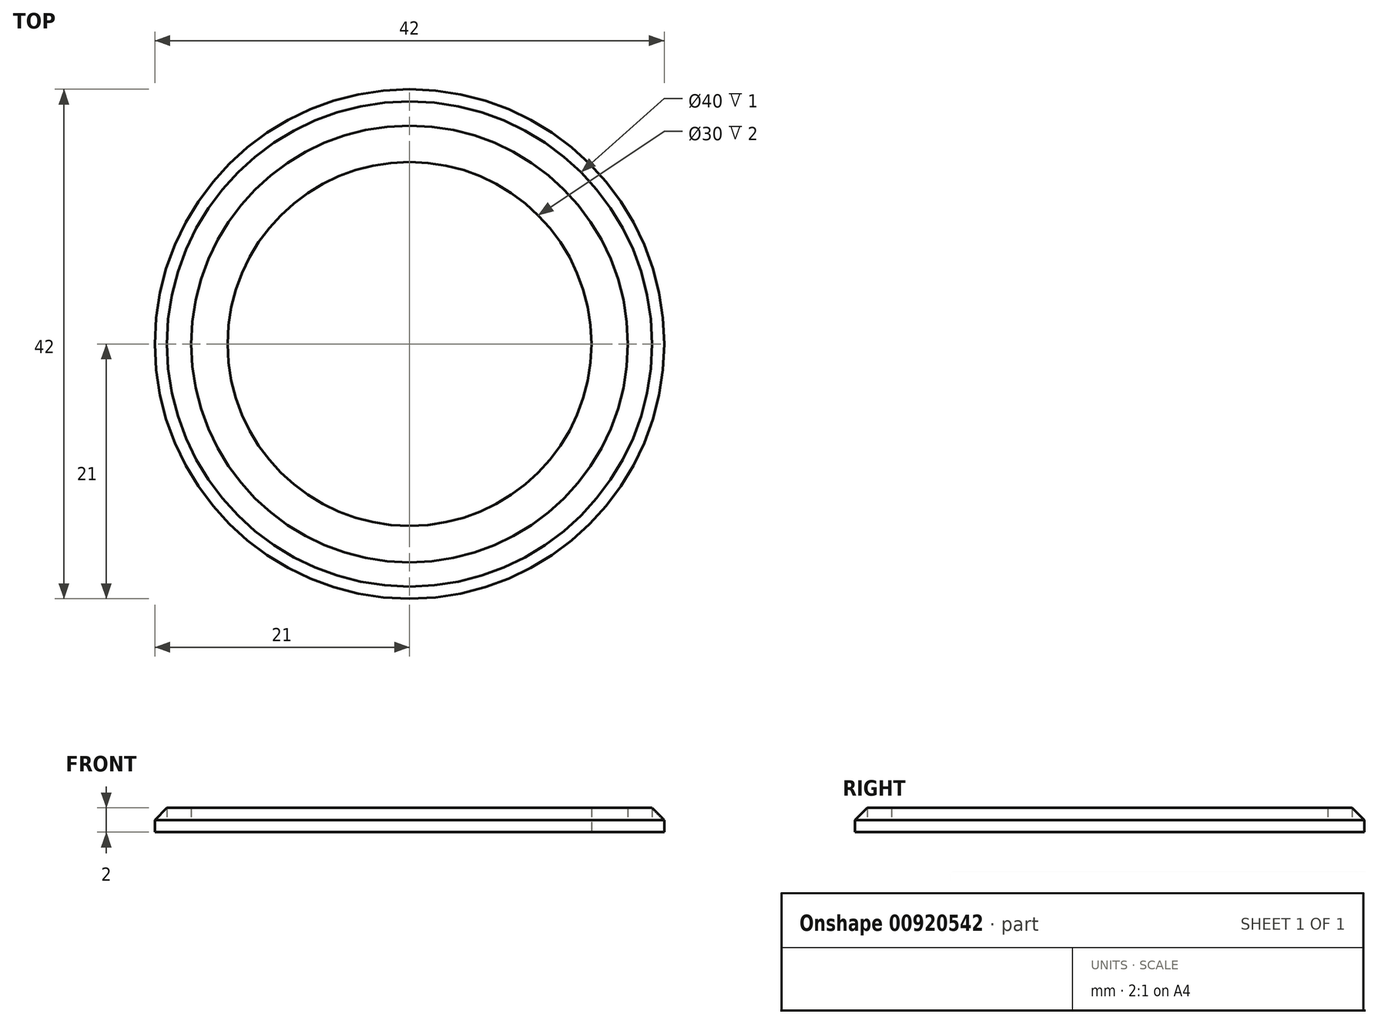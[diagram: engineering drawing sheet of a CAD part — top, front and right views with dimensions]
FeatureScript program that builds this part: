
annotation { "Feature Type Name" : "Feature", "Feature Type Description" : "" }
export const myFeature = defineFeature(function(context is Context, id is Id, definition is map)
    precondition{}
    {
        {
            var Q0;
            Q0=qCreatedBy(makeId("Top.planeOp"),FACE);
            var sketch = newSketch(context, id + "F0", { "sketchPlane" : qUnion([Q0])});
            skCircle(sketch, "E0", {"center": v(0, 0) * mm, "radius": 21 * mm});
            skCircle(sketch, "E1", {"center": v(0, 0) * mm, "radius": 20 * mm});
            skCircle(sketch, "E2", {"center": v(0, 0) * mm, "radius": 18 * mm});
            skCircle(sketch, "E3", {"center": v(0, 0) * mm, "radius": 15 * mm});
            skLineSegment(sketch, "E4", {"start": v(-21, 0) * mm, "end": v(-18, 0) * mm});
            skLineSegment(sketch, "E5", {"start": v(-18, 0) * mm, "end": v(-17.3, 0) * mm});
            skLineSegment(sketch, "E6", {"start": v(-16.5, 0) * mm, "end": v(-16.5, -2) * mm, "construction": true});
            skLineSegment(sketch, "E7", {"start": v(-16.5, -2) * mm, "end": v(-15.5, -2) * mm});
            skLineSegment(sketch, "E8", {"start": v(-15.5, -2) * mm, "end": v(-15.7, 0) * mm});
            skLineSegment(sketch, "E9.MirrorCS", {"start": v(-16.5, -2) * mm, "end": v(-17.5, -2) * mm});
            skLineSegment(sketch, "E10.MirrorCS", {"start": v(-17.5, -2) * mm, "end": v(-17.3, 0) * mm});
            skLineSegment(sketch, "E11.trimOffspring", {"start": v(-15.7, 0) * mm, "end": v(-15, 0) * mm});
            skLineSegment(sketch, "E12", {"start": v(0, 0) * mm, "end": v(0, -15) * mm, "construction": true});
            skLineSegment(sketch, "E13.MirrorCS", {"start": v(15.5, -2) * mm, "end": v(15.7, 0) * mm});
            skLineSegment(sketch, "E14.MirrorCS", {"start": v(16.5, -2) * mm, "end": v(15.5, -2) * mm});
            skLineSegment(sketch, "E15.MirrorCS", {"start": v(16.5, -2) * mm, "end": v(17.5, -2) * mm});
            skLineSegment(sketch, "E16.MirrorCS", {"start": v(17.5, -2) * mm, "end": v(17.3, 0) * mm});
            skLineSegment(sketch, "E17.MirrorCS", {"start": v(21, 0) * mm, "end": v(18, 0) * mm});
            skLineSegment(sketch, "E18.MirrorCS", {"start": v(18, 0) * mm, "end": v(17.3, 0) * mm});
            skLineSegment(sketch, "E19.MirrorCS", {"start": v(15.7, 0) * mm, "end": v(15, 0) * mm});
            skSolve(sketch);
        }
        {
            var Q0;
            {var subQ0=sQuery(id+"F0.wireOp",EDGE,"E4");var subQ1=sQuery(id+"F0.wireOp",EDGE,"E0");var subQ2=makeQuery(id+"F0.imprint","INTERSECT",VERTEX,{"derivedFrom":[subQ1,subQ0]});Q0=makeQuery(id+"F0.imprint","IMPRINT",FACE,{"disambiguationData":[TD([[makeQuery(id+"F0.imprint","IMPRINT",EDGE,{"disambiguationData":[TD([[subQ2,1.0]])],"derivedFrom":subQ1}),1.0]])]});}
            extrude(context, id + "F1", {"entities" : qUnion([Q0]), "depth" : 2 * mm, "offsetDistance" : 25 * mm});
        }
        {
            var Q0;
            {var subQ0=sQuery(id+"F0.wireOp",EDGE,"E4");var subQ1=sQuery(id+"F0.wireOp",EDGE,"E1");var subQ2=makeQuery(id+"F0.imprint","INTERSECT",VERTEX,{"derivedFrom":[subQ1,subQ0]});Q0=makeQuery(id+"F0.imprint","IMPRINT",FACE,{"disambiguationData":[TD([[makeQuery(id+"F0.imprint","IMPRINT",EDGE,{"disambiguationData":[TD([[subQ2,1.0]])],"derivedFrom":subQ1}),1.0]])]});}
            extrude(context, id + "F2", {"entities" : qUnion([Q0]), "operationType" : NewBodyOperationType.ADD, "depth" : 1 * mm, "offsetDistance" : 25 * mm});
        }
        {
            var Q0;
            {var subQ1=sQuery(id+"F0.wireOp",EDGE,"E5");Q0=makeQuery(id+"F0.imprint","IMPRINT",FACE,{"disambiguationData":[TD([[makeQuery(id+"F0.imprint","IMPRINT",EDGE,{"derivedFrom":subQ1}),1.0]])]});}
            extrude(context, id + "F3", {"entities" : qUnion([Q0]), "operationType" : NewBodyOperationType.ADD, "depth" : 2 * mm, "offsetDistance" : 25 * mm});
        }
        {
            var Q0;
            {var subQ1=sQuery(id+"F0.wireOp",EDGE,"E5");Q0=makeQuery(id+"F0.imprint","IMPRINT",FACE,{"disambiguationData":[TD([[makeQuery(id+"F0.imprint","IMPRINT",EDGE,{"derivedFrom":subQ1}),-1.0]])]});}
            extrude(context, id + "F4", {"entities" : qUnion([Q0]), "depth" : 2 * mm, "offsetDistance" : 25 * mm});
        }
        {
            var Q0;
            {var subQ0=sQuery(id+"F0.wireOp",EDGE,"E4");var subQ1=sQuery(id+"F0.wireOp",EDGE,"E1");var subQ2=makeQuery(id+"F0.imprint","INTERSECT",VERTEX,{"derivedFrom":[subQ1,subQ0]});Q0=makeQuery(id+"F0.imprint","IMPRINT",FACE,{"disambiguationData":[TD([[makeQuery(id+"F0.imprint","IMPRINT",EDGE,{"disambiguationData":[TD([[subQ2,-1.0]])],"derivedFrom":subQ1}),1.0]])]});}
            extrude(context, id + "F5", {"entities" : qUnion([Q0]), "operationType" : NewBodyOperationType.ADD, "depth" : 1 * mm, "offsetDistance" : 25 * mm});
        }
        {
            var Q0;
            {var subQ0=sQuery(id+"F0.wireOp",EDGE,"E4");var subQ1=sQuery(id+"F0.wireOp",EDGE,"E0");var subQ2=makeQuery(id+"F0.imprint","INTERSECT",VERTEX,{"derivedFrom":[subQ1,subQ0]});Q0=makeQuery(id+"F0.imprint","IMPRINT",FACE,{"disambiguationData":[TD([[makeQuery(id+"F0.imprint","IMPRINT",EDGE,{"disambiguationData":[TD([[subQ2,-1.0]])],"derivedFrom":subQ1}),1.0]])]});}
            extrude(context, id + "F6", {"entities" : qUnion([Q0]), "operationType" : NewBodyOperationType.ADD, "depth" : 2 * mm, "offsetDistance" : 25 * mm});
        }
        {
            var Q0;
            Q0=makeQuery(id+"F6.opExtrude","CAP_EDGE",EDGE,{"disambiguationData":[OSD([sQuery(id+"F0.wireOp",EDGE,"E0")])],"isStart":false});
            var Q1;
            Q1=makeQuery(id+"F1.opExtrude","CAP_EDGE",EDGE,{"disambiguationData":[OSD([sQuery(id+"F0.wireOp",EDGE,"E0")])],"isStart":false});
            chamfer(context, id + "F7", {"entities" : qUnion([Q0, Q1]), "width" : 1 * mm, "tangentPropagation" : true});
        }
    });
